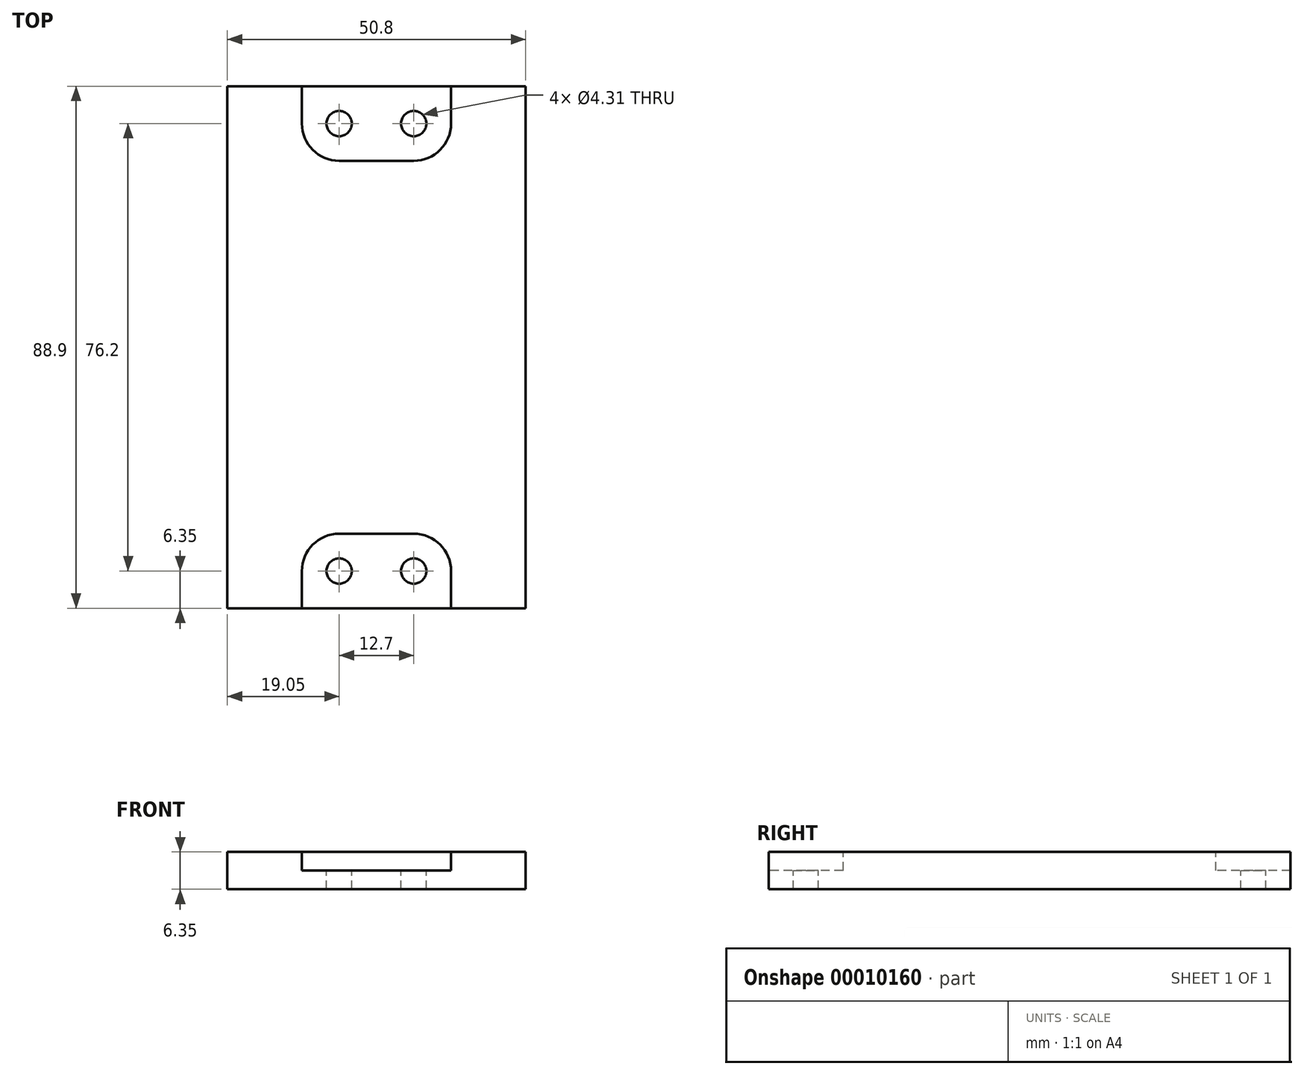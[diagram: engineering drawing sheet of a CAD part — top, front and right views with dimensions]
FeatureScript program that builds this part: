
annotation { "Feature Type Name" : "Feature", "Feature Type Description" : "" }
export const myFeature = defineFeature(function(context is Context, id is Id, definition is map)
    precondition{}
    {
        {
            var Q0;
            Q0=qCreatedBy(makeId("Top.planeOp"),FACE);
            var sketch = newSketch(context, id + "F0", { "sketchPlane" : qUnion([Q0])});
            skLineSegment(sketch, "E0.bottom", {"start": v(25.4, 44.45) * mm, "end": v(-25.4, 44.45) * mm});
            skLineSegment(sketch, "E0.top", {"start": v(25.4, -44.45) * mm, "end": v(-25.4, -44.45) * mm});
            skLineSegment(sketch, "E0.left", {"start": v(25.4, 44.45) * mm, "end": v(25.4, -44.45) * mm});
            skLineSegment(sketch, "E0.right", {"start": v(-25.4, 44.45) * mm, "end": v(-25.4, -44.45) * mm});
            skPoint(sketch, "E0.middle", {"position": v(0, 0) * mm});
            skSolve(sketch);
        }
        {
            var Q0;
            Q0 = qSketchRegion(id + "F0", true);
            extrude(context, id + "F1", {"entities" : qUnion([Q0]), "depth" : 6.35 * mm});
        }
        {
            var Q0;
            Q0=makeQuery(id+"F1.opExtrude","CAP_FACE",FACE,{"disambiguationData":[OSD([sQuery(id+"F0.wireOp",EDGE,"E0.bottom"),sQuery(id+"F0.wireOp",EDGE,"E0.top"),sQuery(id+"F0.wireOp",EDGE,"E0.left"),sQuery(id+"F0.wireOp",EDGE,"E0.right")])],"isStart":false});
            var sketch = newSketch(context, id + "F2", { "sketchPlane" : qUnion([Q0])});
            skCircle(sketch, "E1", {"center": v(6.35, 38.1) * mm, "radius": 2.15 * mm});
            skCircle(sketch, "E2.0.1.0", {"center": v(6.35, -38.1) * mm, "radius": 2.15 * mm});
            skCircle(sketch, "E2.1.0.0", {"center": v(-6.35, 38.1) * mm, "radius": 2.15 * mm});
            skCircle(sketch, "E2.1.1.0", {"center": v(-6.35, -38.1) * mm, "radius": 2.15 * mm});
            skLineSegment(sketch, "E2.direction1", {"start": v(6.35, 38.1) * mm, "end": v(-6.35, 38.1) * mm, "construction": true});
            skLineSegment(sketch, "E2.direction2", {"start": v(6.35, 38.1) * mm, "end": v(6.35, -38.1) * mm, "construction": true});
            skSolve(sketch);
        }
        {
            var Q0;
            Q0 = qSketchRegion(id + "F2", true);
            extrude(context, id + "F3", {"entities" : qUnion([Q0]), "operationType" : NewBodyOperationType.REMOVE, "endBound" : BoundingType.UP_TO_NEXT, "oppositeDirection" : true, "depth" : 25.4 * mm});
        }
        {
            var Q0;
            Q0=makeQuery(id+"F1.opExtrude","CAP_FACE",FACE,{"disambiguationData":[OSD([sQuery(id+"F0.wireOp",EDGE,"E0.bottom"),sQuery(id+"F0.wireOp",EDGE,"E0.top"),sQuery(id+"F0.wireOp",EDGE,"E0.left"),sQuery(id+"F0.wireOp",EDGE,"E0.right")])],"isStart":false});
            var sketch = newSketch(context, id + "F4", { "sketchPlane" : qUnion([Q0])});
            skLineSegment(sketch, "E3.bottom", {"start": v(6.35, -31.75) * mm, "end": v(-6.35, -31.75) * mm});
            skLineSegment(sketch, "E3.top", {"start": v(12.7, -44.45) * mm, "end": v(-12.7, -44.45) * mm});
            skLineSegment(sketch, "E3.left", {"start": v(12.7, -38.1) * mm, "end": v(12.7, -44.45) * mm});
            skLineSegment(sketch, "E3.right", {"start": v(-12.7, -38.1) * mm, "end": v(-12.7, -44.45) * mm});
            skPoint(sketch, "E3.middle", {"position": v(0, -38.1) * mm});
            skPoint(sketch, "E4.visualSharp", {"position": v(-12.7, -31.75) * mm});
            skArc(sketch, "E4.filletArc", {"start": v(-6.35, -31.75) * mm, "mid": v(-10.84, -33.6) * mm, "end": v(-12.7, -38.1) * mm});
            skPoint(sketch, "E5.visualSharp", {"position": v(12.7, -31.75) * mm});
            skArc(sketch, "E5.filletArc", {"start": v(12.7, -38.1) * mm, "mid": v(10.84, -33.6) * mm, "end": v(6.35, -31.75) * mm});
            skLineSegment(sketch, "E6.bottom", {"start": v(12.7, 44.45) * mm, "end": v(-12.7, 44.45) * mm});
            skLineSegment(sketch, "E6.top", {"start": v(6.35, 31.75) * mm, "end": v(-6.35, 31.75) * mm});
            skLineSegment(sketch, "E6.left", {"start": v(12.7, 44.45) * mm, "end": v(12.7, 38.1) * mm});
            skLineSegment(sketch, "E6.right", {"start": v(-12.7, 44.45) * mm, "end": v(-12.7, 38.1) * mm});
            skPoint(sketch, "E6.middle", {"position": v(0, 38.1) * mm});
            skPoint(sketch, "E7.visualSharp", {"position": v(-12.7, 31.75) * mm});
            skArc(sketch, "E7.filletArc", {"start": v(-12.7, 38.1) * mm, "mid": v(-10.84, 33.6) * mm, "end": v(-6.35, 31.75) * mm});
            skPoint(sketch, "E8.visualSharp", {"position": v(12.7, 31.75) * mm});
            skArc(sketch, "E8.filletArc", {"start": v(6.35, 31.75) * mm, "mid": v(10.84, 33.6) * mm, "end": v(12.7, 38.1) * mm});
            skSolve(sketch);
        }
        {
            var Q0;
            Q0 = qSketchRegion(id + "F4", true);
            extrude(context, id + "F5", {"entities" : qUnion([Q0]), "operationType" : NewBodyOperationType.REMOVE, "oppositeDirection" : true, "depth" : 3.17 * mm});
        }
    });
